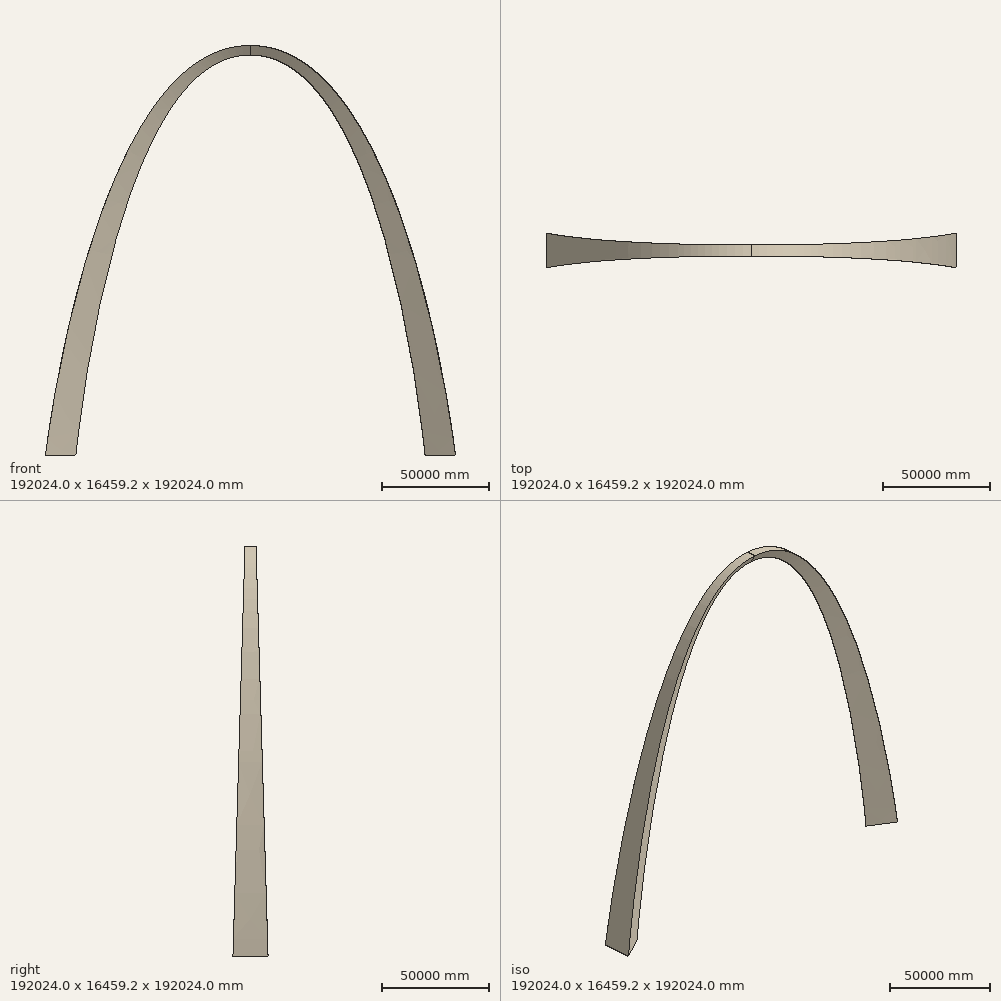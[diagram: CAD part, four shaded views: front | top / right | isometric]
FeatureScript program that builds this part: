
annotation { "Feature Type Name" : "Feature", "Feature Type Description" : "" }
export const myFeature = defineFeature(function(context is Context, id is Id, definition is map)
    precondition{}
    {
        {
            var Q0;
            Q0=qCreatedBy(makeId("Top.planeOp"),FACE);
            var sketch = newSketch(context, id + "F0", { "sketchPlane" : qUnion([Q0])});
            skLineSegment(sketch, "E0", {"start": v(96012, 8229.6) * mm, "end": v(96012, -8229.6) * mm});
            skLineSegment(sketch, "E1", {"start": v(96012, 8229.6) * mm, "end": v(81757.91, 0) * mm});
            skLineSegment(sketch, "E2", {"start": v(81757.91, 0) * mm, "end": v(96012, -8229.6) * mm});
            skSolve(sketch);
        }
        {
            var Q0;
            Q0=qCreatedBy(makeId("Right.planeOp"),FACE);
            var sketch = newSketch(context, id + "F1", { "sketchPlane" : qUnion([Q0])});
            skLineSegment(sketch, "E3", {"start": v(-2590.8, 192024) * mm, "end": v(2590.8, 192024) * mm});
            skLineSegment(sketch, "E4", {"start": v(-2590.8, 192024) * mm, "end": v(0, 187536.6) * mm});
            skLineSegment(sketch, "E5", {"start": v(0, 187536.6) * mm, "end": v(2590.8, 192024) * mm});
            skSolve(sketch);
        }
        {
            var Q0;
            Q0=qCreatedBy(makeId("Front.planeOp"),FACE);
            var sketch = newSketch(context, id + "F2", { "sketchPlane" : qUnion([Q0])});
            skPoint(sketch, "E6", {"position": v(76200, 35545.78) * mm});
            skPoint(sketch, "E7", {"position": v(73152, 52459.13) * mm});
            skPoint(sketch, "E8", {"position": v(70104, 67757.04) * mm});
            skPoint(sketch, "E9", {"position": v(67056, 81588.86) * mm});
            skPoint(sketch, "E10", {"position": v(64008, 94092.98) * mm});
            skPoint(sketch, "E11", {"position": v(60960, 105384.6) * mm});
            skPoint(sketch, "E12", {"position": v(53340, 129018.8) * mm});
            skPoint(sketch, "E13", {"position": v(45720, 147194.93) * mm});
            skPoint(sketch, "E14", {"position": v(38100, 161016.7) * mm});
            skPoint(sketch, "E15", {"position": v(30480, 171331.13) * mm});
            skPoint(sketch, "E16", {"position": v(24384, 177485.04) * mm});
            skPoint(sketch, "E17", {"position": v(18288, 182038.75) * mm});
            skPoint(sketch, "E18", {"position": v(81758.03, 0) * mm});
            skPoint(sketch, "E19", {"position": v(0, 187536.73) * mm});
            skPoint(sketch, "E20", {"position": v(6096, 187002.12) * mm});
            skPoint(sketch, "E21", {"position": v(12192, 185170.57) * mm});
            skFitSpline(sketch, "E22", {"points": [v(81758.03, 0) * mm, v(76200, 35545.78) * mm, v(73152, 52459.13) * mm, v(70104, 67757.04) * mm, v(67056, 81588.86) * mm, v(64008, 94092.98) * mm, v(60960, 105384.6) * mm, v(53340, 129018.8) * mm, v(45720, 147194.93) * mm, v(38100, 161016.7) * mm, v(30480, 171331.13) * mm, v(24384, 177485.04) * mm, v(18288, 182038.75) * mm, v(12192, 185170.57) * mm, v(6096, 187002.12) * mm, v(0, 187536.73) * mm], "startDerivative": vector(-54562.4, 358026) * mm, "endDerivative": vector(-136364.62, 5889.43) * mm});
            skSolve(sketch);
        }
        {
            var Q0;
            Q0 = qSketchRegion(id + "F1", true);
            var Q1;
            Q1 = qSketchRegion(id + "F0", true);
            var Q2;
            Q2 = qConstructionFilter(qBodyType(qCreatedBy(id + "F2" ,EDGE), BodyType.WIRE), ConstructionObject.NO);
            var Q3;
            Q3=sQuery(id+"F2.wireOp",VERTEX,"E19");
            var Q4;
            Q4=sQuery(id+"F2.wireOp",VERTEX,"E18");
            loft(context, id + "F3", {"startCondition" : LoftEndDerivativeType.NORMAL_TO_PROFILE, "startMagnitude" : 2.05, "endCondition" : LoftEndDerivativeType.NORMAL_TO_PROFILE, "endMagnitude" : 0, "sheetProfilesArray" : [{ "sheetProfileEntities" : qUnion([Q0]) }, { "sheetProfileEntities" : qUnion([Q1]) }], "guidesArray" : [{ "guideEntities" : qUnion([Q2]), "guideDerivativeType" : LoftGuideDerivativeType.DEFAULT, "guideDerivativeMagnitude" : 1 }], "connections" : [{ "connectionEntities" : qUnion([Q3, Q4]), "connectionEdgeQueries" : qUnion([]), "connectionEdgeParameters" : [] }]});
        }
        {
            var Q0;
            Q0=makeQuery(id+"F3.opLoft","SWEPT_BODY",BODY,{"disambiguationData":[OSD([makeQuery(id+"F0.imprint","IMPRINT",FACE,{"disambiguationData":[TD([[makeQuery(id+"F0.imprint","IMPRINT",EDGE,{"derivedFrom":sQuery(id+"F0.wireOp",EDGE,"E0")}),-1.0]])]}),makeQuery(id+"F1.imprint","IMPRINT",FACE,{"disambiguationData":[TD([[makeQuery(id+"F1.imprint","IMPRINT",EDGE,{"derivedFrom":sQuery(id+"F1.wireOp",EDGE,"E3")}),-1.0]])]})])]});
            var Q1;
            Q1=makeQuery(id+"F3.opLoft","CAP_FACE",FACE,{"disambiguationData":[OSD([makeQuery(id+"F1.imprint","IMPRINT",FACE,{"disambiguationData":[TD([[makeQuery(id+"F1.imprint","IMPRINT",EDGE,{"derivedFrom":sQuery(id+"F1.wireOp",EDGE,"E3")}),-1.0]])]})])],"isStart":true});
            mirror(context, id + "F4", {"operationType" : NewBodyOperationType.ADD, "entities" : qUnion([Q0]), "mirrorPlane" : qUnion([Q1])});
        }
    });
